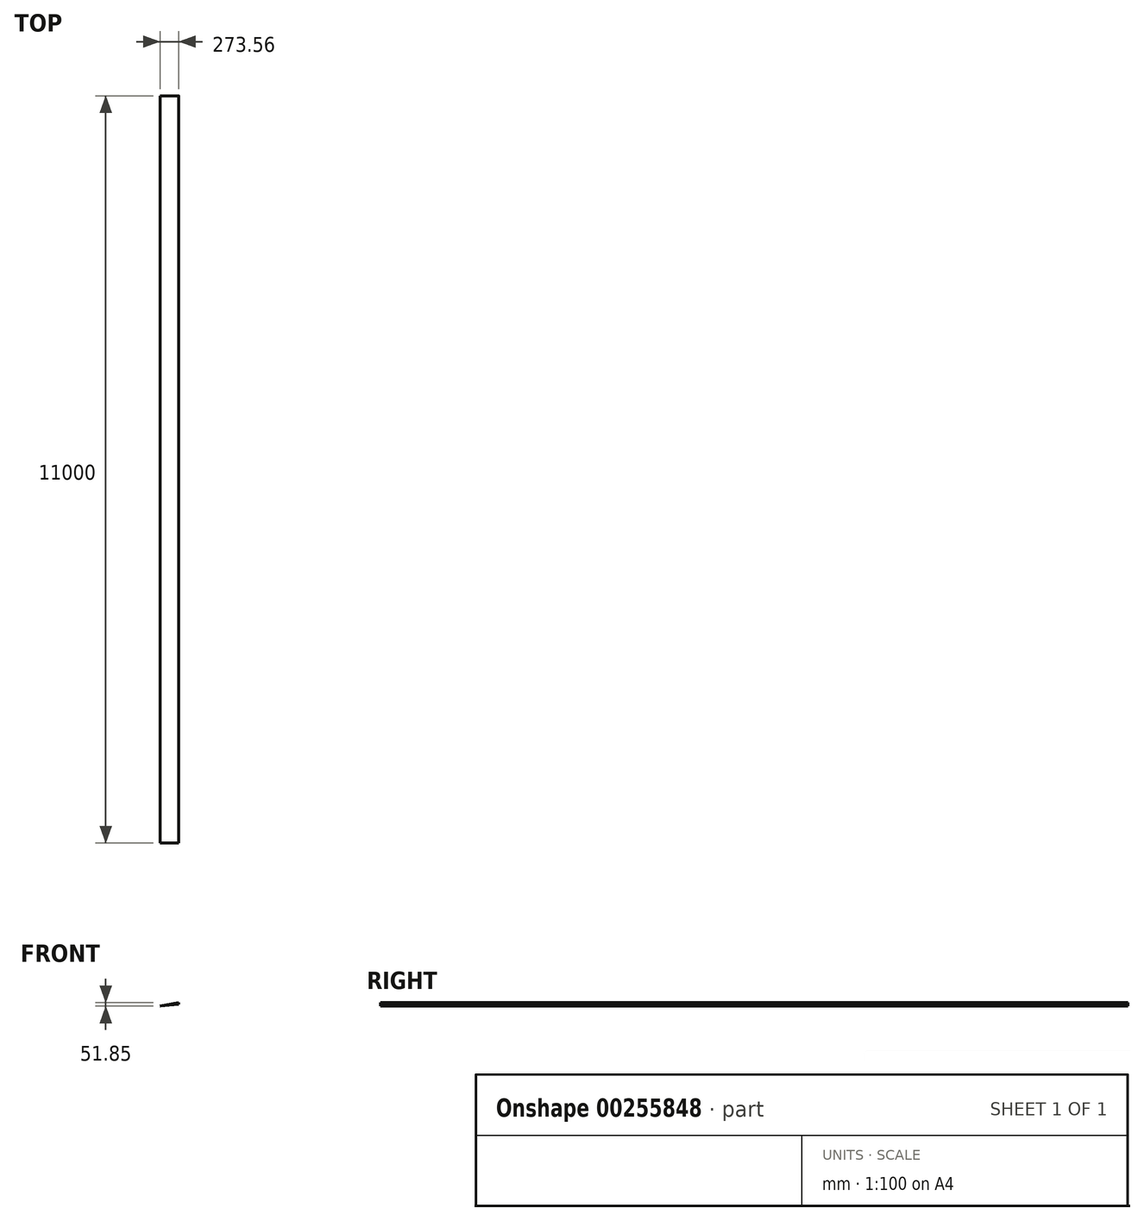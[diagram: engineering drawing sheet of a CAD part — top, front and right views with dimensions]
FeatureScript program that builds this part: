
annotation { "Feature Type Name" : "Feature", "Feature Type Description" : "" }
export const myFeature = defineFeature(function(context is Context, id is Id, definition is map)
    precondition{}
    {
        {
            var Q0;
            Q0=qCreatedBy(makeId("Front.planeOp"),FACE);
            var sketch = newSketch(context, id + "F0", { "sketchPlane" : qUnion([Q0])});
            skCircle(sketch, "E0", {"center": v(0, 0) * mm, "radius": 275 * mm});
            skLineSegment(sketch, "E1", {"start": v(0, 0) * mm, "end": v(270.07, 51.85) * mm});
            skLineSegment(sketch, "E2", {"start": v(0, 0) * mm, "end": v(273.56, 28.11) * mm});
            skSolve(sketch);
        }
        {
            var Q0;
            {var subQ0=sQuery(id+"F0.wireOp",EDGE,"E1");Q0=makeQuery(id+"F0.imprint","IMPRINT",FACE,{"disambiguationData":[TD([[makeQuery(id+"F0.imprint","IMPRINT",EDGE,{"derivedFrom":subQ0}),-1.0]])]});}
            extrude(context, id + "F1", {"entities" : qUnion([Q0]), "endBound" : BoundingType.SYMMETRIC, "depth" : 11000 * mm});
        }
    });
